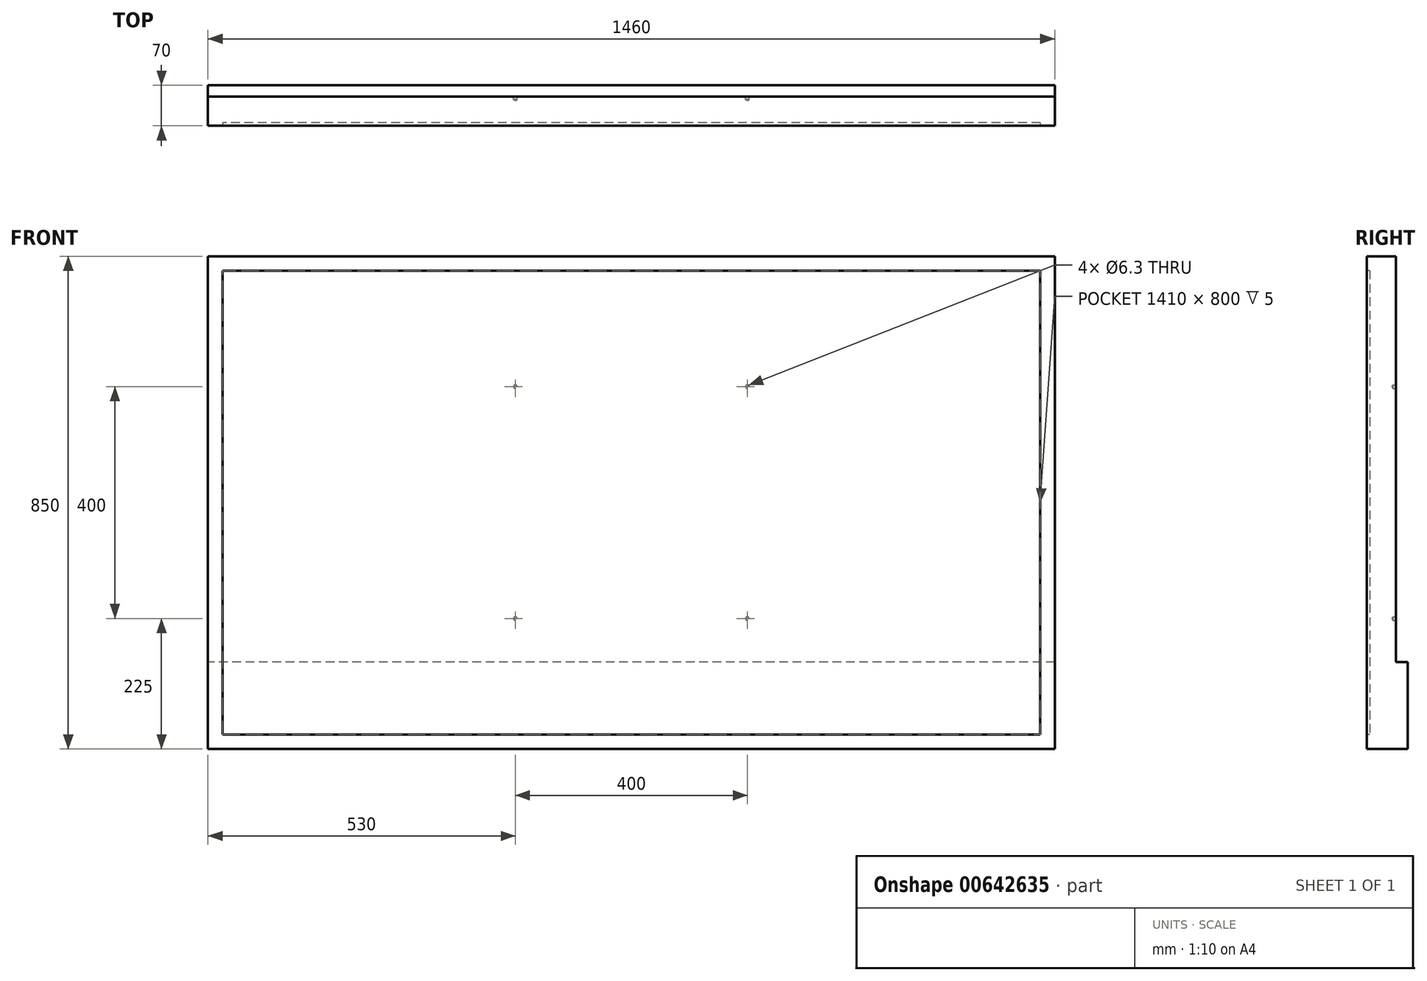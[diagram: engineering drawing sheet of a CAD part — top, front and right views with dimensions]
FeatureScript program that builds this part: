
annotation { "Feature Type Name" : "Feature", "Feature Type Description" : "" }
export const myFeature = defineFeature(function(context is Context, id is Id, definition is map)
    precondition{}
    {
        {
            var Q0;
            Q0=qCreatedBy(makeId("Front.planeOp"),FACE);
            var sketch = newSketch(context, id + "F0", { "sketchPlane" : qUnion([Q0])});
            skLineSegment(sketch, "E0.bottom", {"start": v(730, 425) * mm, "end": v(-730, 425) * mm});
            skLineSegment(sketch, "E0.top", {"start": v(730, -425) * mm, "end": v(-730, -425) * mm});
            skLineSegment(sketch, "E0.left", {"start": v(730, 425) * mm, "end": v(730, -425) * mm});
            skLineSegment(sketch, "E0.right", {"start": v(-730, 425) * mm, "end": v(-730, -425) * mm});
            skPoint(sketch, "E0.middle", {"position": v(0, 0) * mm});
            skSolve(sketch);
        }
        {
            var Q0;
            Q0=makeQuery(id+"F0.imprint","IMPRINT",FACE,{"disambiguationData":[TD([[makeQuery(id+"F0.imprint","IMPRINT",EDGE,{"derivedFrom":sQuery(id+"F0.wireOp",EDGE,"E0.bottom")}),1.0]])]});
            extrude(context, id + "F1", {"entities" : qUnion([Q0]), "depth" : 50 * mm, "offsetDistance" : 25 * mm});
        }
        {
            var Q0;
            Q0=makeQuery(id+"F1.opExtrude","CAP_FACE",FACE,{"disambiguationData":[OSD([sQuery(id+"F0.wireOp",EDGE,"E0.bottom"),sQuery(id+"F0.wireOp",EDGE,"E0.top"),sQuery(id+"F0.wireOp",EDGE,"E0.left"),sQuery(id+"F0.wireOp",EDGE,"E0.right")])],"isStart":false});
            var sketch = newSketch(context, id + "F2", { "sketchPlane" : qUnion([Q0])});
            skLineSegment(sketch, "E1.0", {"start": v(705, 400) * mm, "end": v(-705, 400) * mm});
            skLineSegment(sketch, "E1.1", {"start": v(705, 400) * mm, "end": v(705, -400) * mm});
            skLineSegment(sketch, "E1.2", {"start": v(705, -400) * mm, "end": v(-705, -400) * mm});
            skLineSegment(sketch, "E1.3", {"start": v(-705, 400) * mm, "end": v(-705, -400) * mm});
            skSolve(sketch);
        }
        {
            var Q0;
            Q0=makeQuery(id+"F2.imprint","IMPRINT",FACE,{"disambiguationData":[TD([[makeQuery(id+"F2.imprint","IMPRINT",EDGE,{"derivedFrom":sQuery(id+"F2.wireOp",EDGE,"E1.0")}),1.0]])]});
            extrude(context, id + "F3", {"entities" : qUnion([Q0]), "operationType" : NewBodyOperationType.REMOVE, "oppositeDirection" : true, "depth" : 5 * mm, "offsetDistance" : 25 * mm});
        }
        {
            var Q0;
            Q0=makeQuery(id+"F1.opExtrude","CAP_FACE",FACE,{"disambiguationData":[OSD([sQuery(id+"F0.wireOp",EDGE,"E0.bottom"),sQuery(id+"F0.wireOp",EDGE,"E0.top"),sQuery(id+"F0.wireOp",EDGE,"E0.left"),sQuery(id+"F0.wireOp",EDGE,"E0.right")])],"isStart":true});
            var sketch = newSketch(context, id + "F4", { "sketchPlane" : qUnion([Q0])});
            skLineSegment(sketch, "E2.bottom", {"start": v(200, 200) * mm, "end": v(-200, 200) * mm, "construction": true});
            skLineSegment(sketch, "E2.top", {"start": v(200, -200) * mm, "end": v(-200, -200) * mm, "construction": true});
            skLineSegment(sketch, "E2.left", {"start": v(200, 200) * mm, "end": v(200, -200) * mm, "construction": true});
            skLineSegment(sketch, "E2.right", {"start": v(-200, 200) * mm, "end": v(-200, -200) * mm, "construction": true});
            skPoint(sketch, "E2.middle", {"position": v(0, 0) * mm});
            skLineSegment(sketch, "E3.bottom", {"start": v(-730, -425) * mm, "end": v(730, -425) * mm});
            skLineSegment(sketch, "E3.top", {"start": v(-730, -275) * mm, "end": v(730, -275) * mm});
            skLineSegment(sketch, "E3.left", {"start": v(-730, -425) * mm, "end": v(-730, -275) * mm});
            skLineSegment(sketch, "E3.right", {"start": v(730, -425) * mm, "end": v(730, -275) * mm});
            skSolve(sketch);
        }
        {
            var Q0;
            Q0=sQuery(id+"F4.wireOp",VERTEX,"E2.right.start");
            var Q1;
            Q1=sQuery(id+"F4.wireOp",VERTEX,"E2.bottom.start");
            var Q2;
            Q2=sQuery(id+"F4.wireOp",VERTEX,"E2.left.end");
            var Q3;
            Q3=sQuery(id+"F4.wireOp",VERTEX,"E2.top.end");
            var Q4;
            Q4=makeQuery(id+"F1.opExtrude","SWEPT_BODY",BODY,{"disambiguationData":[OSD([sQuery(id+"F0.wireOp",EDGE,"E0.bottom"),sQuery(id+"F0.wireOp",EDGE,"E0.top"),sQuery(id+"F0.wireOp",EDGE,"E0.left"),sQuery(id+"F0.wireOp",EDGE,"E0.right")])]});
            hole(context, id + "F5", {"style" : HoleStyle.SIMPLE, "endStyle" : HoleEndStyle.BLIND, "holeDiameter" : 6.3 * mm, "majorDiameter" : 5 * mm, "holeDepth" : 5 * mm, "isTappedThrough" : true, "tappedDepth" : 12 * mm, "tapClearance" : 3, "locations" : qUnion([Q0, Q1, Q2, Q3]), "scope" : qUnion([Q4])});
        }
        {
            var Q0;
            Q0=makeQuery(id+"F4.imprint","IMPRINT",FACE,{"disambiguationData":[TD([[makeQuery(id+"F4.imprint","IMPRINT",EDGE,{"derivedFrom":sQuery(id+"F4.wireOp",EDGE,"E3.bottom")}),1.0]])]});
            extrude(context, id + "F6", {"entities" : qUnion([Q0]), "operationType" : NewBodyOperationType.ADD, "depth" : 20 * mm, "offsetDistance" : 25 * mm});
        }
    });
